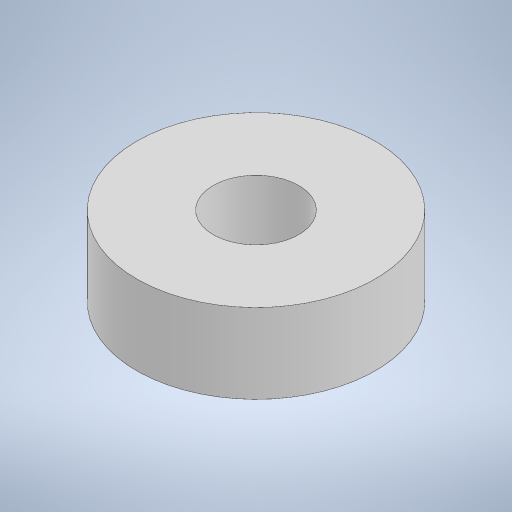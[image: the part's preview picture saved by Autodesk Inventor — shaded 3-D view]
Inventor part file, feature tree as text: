
AUTODESK INVENTOR PART (.ipt)
format: ipt  version: 2024.3 (Build 283343000, 343)  size: 206,848 bytes
history: native  units: mm
features: other x1, extrude x1, sketch x1
ambient origin geometry x8: Origin, YZ Plane, XZ Plane, XY Plane, X Axis, Y Axis, Z Axis, Center Point
bodies: Body1 (feature_tree)
feature tree (3):
  other  "Sólido1"
  extrude  "Extrusión1"  Depth=2.7mm
  sketch  "Boceto1"  dims[d0=2.9mm d1=2.6mm d2=2.7mm d3=0.0mm]
